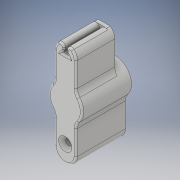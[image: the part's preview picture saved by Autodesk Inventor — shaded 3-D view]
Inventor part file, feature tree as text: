
AUTODESK INVENTOR PART (.ipt)
format: ipt  version: 2019 (Build 230136000, 136)  size: 299,520 bytes
history: native  units: mm
features: fillet x7, extrude x6, sketch x6, chamfer x1, mirror x1
ambient origin geometry x8: Origin, YZ Plane, XZ Plane, XY Plane, X Axis, Y Axis, Z Axis, Center Point
bodies: Solid1 (feature_tree)
feature tree (21):
  extrude  "Extrusion1"  Depth=4.0mm
  extrude  "Extrusion2"  Depth=2.0mm
  extrude  "Extrusion3"  Depth=9.5mm
  fillet  "Fillet1"  Radius=0.1mm
  fillet  "Fillet2"  Radius=6.0mm
  extrude  "Extrusion4"  TaperAngle=0.0deg  [1 undecoded]
  fillet  "Fillet3"  Radius=3.5mm
  fillet  "Fillet4"  Radius=3.5mm
  chamfer  "Chamfer1"  Distance=22.0mm
  fillet  "Fillet5"  Radius=53.0mm
  extrude  "Extrusion5"  Depth=12.0mm
  mirror  "Mirror1"
  extrude  "Extrusion6"  Depth=22.0mm TaperAngle=0.0deg
  fillet  "Fillet6"  Radius=6.0mm
  fillet  "Fillet7"  Radius=6.0mm
  sketch  "Sketch1"  dims[d0=31.0mm d1=4.0mm]
  sketch  "Sketch2"  dims[d2=7.5mm d3=2.0mm]
  sketch  "Sketch4"  dims[d4=2.0mm d5=9.5mm d6=0.1mm d7=6.0mm d8=0.0mm]
  sketch  "Sketch5"  dims[d9=31.0mm d10=4.0mm d11=7.5mm d12=2.0mm d13=2.0mm d14=9.5mm d15=0.1mm d16=6.0mm d17=0.0mm d19=3.5mm d21=3.5mm d22=22.0mm d23=0.0mm d48=53.0mm]
  sketch  "Sketch6"  dims[d49=15.0mm d50=12.0mm]
  sketch  "Sketch7"  dims[d51=30.0mm d52=22.0mm d53=0.0mm d54=6.0mm d55=6.0mm d56=0.7mm d57=0.7mm d58=20.0mm d59=0.0mm d60=2.0mm d61=1.0mm d62=2.0mm d63=2.0mm d64=45.0deg d65=8.0mm d66=5.0mm d67=7.0mm d68=2.5mm d69=6.0mm d70=0.0mm d71=5.0mm d72=2.0mm d73=5.0mm d74=2.0mm d75=6.0mm d76=0.0mm d77=2.0mm d78=2.0mm d79=1.0mm d80=1.0mm]
note: 1 required parameter value undecoded (feature->parameter linkage not recoverable at this tier; creation-order binding heuristic only, values carry confidence <= 0.55)
